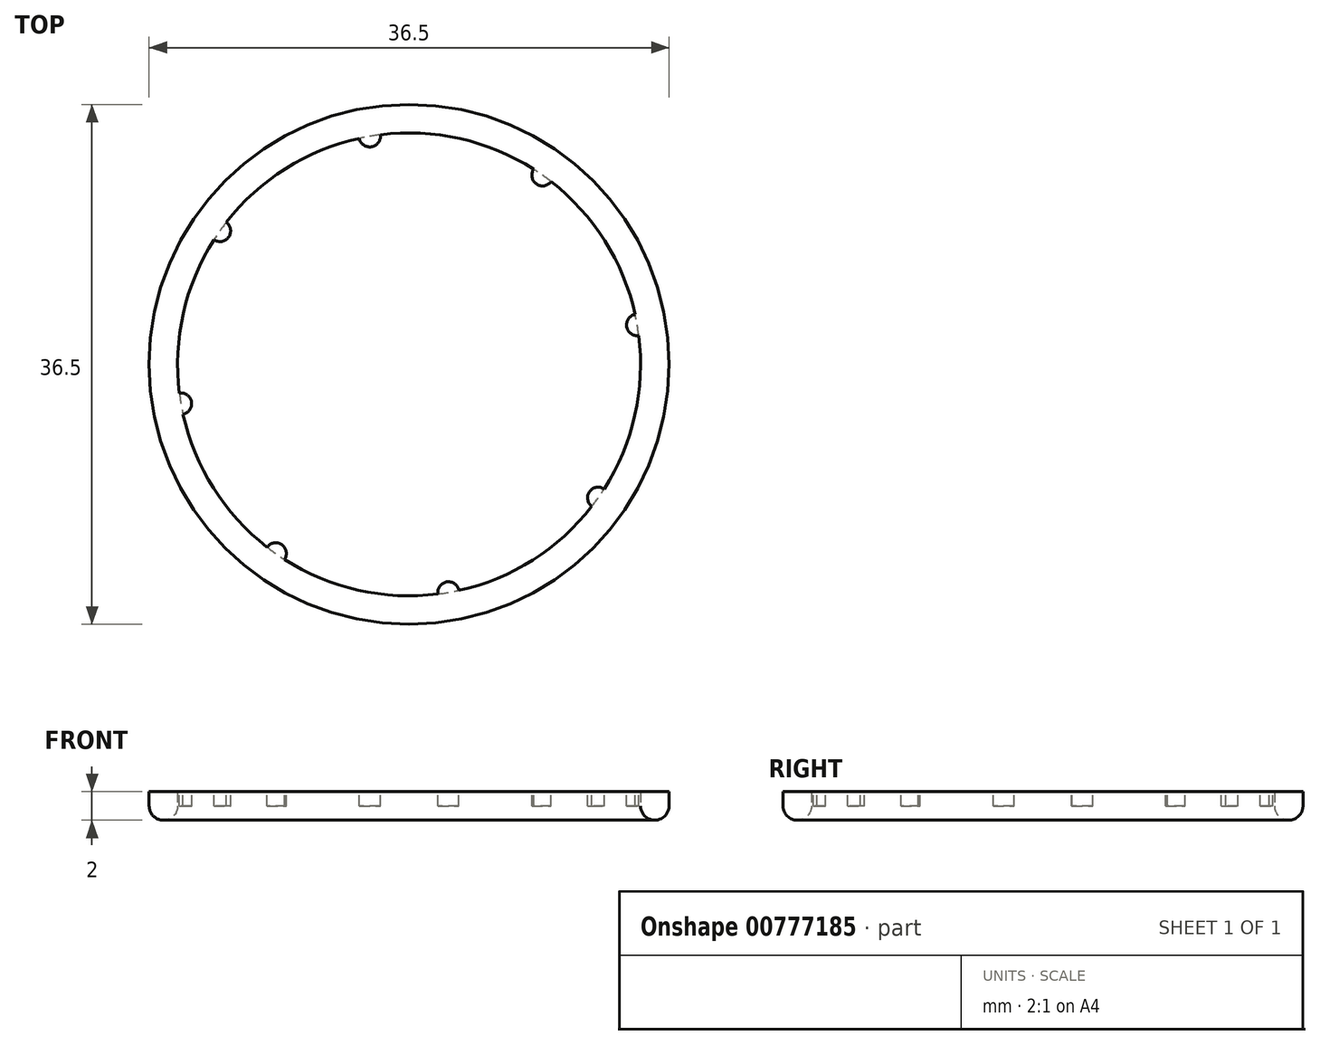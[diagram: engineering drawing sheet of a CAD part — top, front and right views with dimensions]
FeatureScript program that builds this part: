
annotation { "Feature Type Name" : "Feature", "Feature Type Description" : "" }
export const myFeature = defineFeature(function(context is Context, id is Id, definition is map)
    precondition{}
    {
        {
            var Q0;
            Q0=qCreatedBy(makeId("Top.planeOp"),FACE);
            var sketch = newSketch(context, id + "F0", { "sketchPlane" : qUnion([Q0])});
            skCircle(sketch, "E0", {"center": v(0, 0) * mm, "radius": 16.25 * mm});
            skCircle(sketch, "E1.0", {"center": v(0, 0) * mm, "radius": 18.25 * mm});
            skSolve(sketch);
        }
        {
            var Q0;
            Q0=makeQuery(id+"F0.imprint","IMPRINT",FACE,{"disambiguationData":[TD([[makeQuery(id+"F0.imprint","IMPRINT",EDGE,{"derivedFrom":sQuery(id+"F0.wireOp",EDGE,"E0")}),-1.0]])]});
            extrude(context, id + "F1", {"entities" : qUnion([Q0]), "depth" : 2 * mm, "offsetDistance" : 25 * mm});
        }
        {
            var Q0;
            Q0=makeQuery(id+"F1.opExtrude","CAP_FACE",FACE,{"disambiguationData":[OSD([sQuery(id+"F0.wireOp",EDGE,"E0"),sQuery(id+"F0.wireOp",EDGE,"E1.0")])],"isStart":false});
            var sketch = newSketch(context, id + "F2", { "sketchPlane" : qUnion([Q0])});
            skCircle(sketch, "E2", {"center": v(-13.28, 9.37) * mm, "radius": 0.75 * mm});
            skCircle(sketch, "E3.1.0", {"center": v(-16.01, -2.76) * mm, "radius": 0.75 * mm});
            skCircle(sketch, "E3.2.0", {"center": v(-9.37, -13.28) * mm, "radius": 0.75 * mm});
            skPoint(sketch, "E3.center", {"position": v(0, 0) * mm});
            skCircle(sketch, "E4.1.3.0", {"center": v(2.76, -16.01) * mm, "radius": 0.75 * mm});
            skCircle(sketch, "E4.1.4.0", {"center": v(13.28, -9.37) * mm, "radius": 0.75 * mm});
            skCircle(sketch, "E5.1.5.0", {"center": v(16.01, 2.76) * mm, "radius": 0.75 * mm});
            skCircle(sketch, "E5.1.6.0", {"center": v(9.37, 13.28) * mm, "radius": 0.75 * mm});
            skCircle(sketch, "E5.1.7.0", {"center": v(-2.76, 16.01) * mm, "radius": 0.75 * mm});
            skSolve(sketch);
        }
        {
            var Q0;
            {var subQ0=sQuery(id+"F2.wireOp",EDGE,"E5.1.5.0");var subQ1=makeQuery(id+"F1.opExtrude","CAP_EDGE",EDGE,{"disambiguationData":[OSD([sQuery(id+"F0.wireOp",EDGE,"E0")])],"isStart":false});var subQ2=makeQuery(id+"F2.imprint","INTERSECT",VERTEX,{"disambiguationData":[OD(0.0)],"derivedFrom":[subQ1,subQ0]});Q0=makeQuery(id+"F2.imprint","IMPRINT",FACE,{"disambiguationData":[TD([[makeQuery(id+"F2.imprint","IMPRINT",EDGE,{"disambiguationData":[TD([[subQ2,1.0]])],"derivedFrom":subQ0}),1.0]])]});}
            var Q1;
            {var subQ0=sQuery(id+"F2.wireOp",EDGE,"E4.1.4.0");var subQ1=makeQuery(id+"F1.opExtrude","CAP_EDGE",EDGE,{"disambiguationData":[OSD([sQuery(id+"F0.wireOp",EDGE,"E0")])],"isStart":false});var subQ2=makeQuery(id+"F2.imprint","INTERSECT",VERTEX,{"disambiguationData":[OD(0.0)],"derivedFrom":[subQ1,subQ0]});Q1=makeQuery(id+"F2.imprint","IMPRINT",FACE,{"disambiguationData":[TD([[makeQuery(id+"F2.imprint","IMPRINT",EDGE,{"disambiguationData":[TD([[subQ2,1.0]])],"derivedFrom":subQ0}),1.0]])]});}
            var Q2;
            {var subQ0=sQuery(id+"F2.wireOp",EDGE,"E4.1.3.0");var subQ1=makeQuery(id+"F1.opExtrude","CAP_EDGE",EDGE,{"disambiguationData":[OSD([sQuery(id+"F0.wireOp",EDGE,"E0")])],"isStart":false});var subQ2=makeQuery(id+"F2.imprint","INTERSECT",VERTEX,{"disambiguationData":[OD(0.0)],"derivedFrom":[subQ1,subQ0]});Q2=makeQuery(id+"F2.imprint","IMPRINT",FACE,{"disambiguationData":[TD([[makeQuery(id+"F2.imprint","IMPRINT",EDGE,{"disambiguationData":[TD([[subQ2,1.0]])],"derivedFrom":subQ0}),1.0]])]});}
            var Q3;
            {var subQ0=sQuery(id+"F2.wireOp",EDGE,"E3.2.0");var subQ1=makeQuery(id+"F1.opExtrude","CAP_EDGE",EDGE,{"disambiguationData":[OSD([sQuery(id+"F0.wireOp",EDGE,"E0")])],"isStart":false});var subQ2=makeQuery(id+"F2.imprint","INTERSECT",VERTEX,{"disambiguationData":[OD(0.0)],"derivedFrom":[subQ1,subQ0]});Q3=makeQuery(id+"F2.imprint","IMPRINT",FACE,{"disambiguationData":[TD([[makeQuery(id+"F2.imprint","IMPRINT",EDGE,{"disambiguationData":[TD([[subQ2,1.0]])],"derivedFrom":subQ0}),1.0]])]});}
            var Q4;
            {var subQ0=sQuery(id+"F2.wireOp",EDGE,"E3.1.0");var subQ1=makeQuery(id+"F1.opExtrude","CAP_EDGE",EDGE,{"disambiguationData":[OSD([sQuery(id+"F0.wireOp",EDGE,"E0")])],"isStart":false});var subQ2=makeQuery(id+"F2.imprint","INTERSECT",VERTEX,{"disambiguationData":[OD(0.0)],"derivedFrom":[subQ1,subQ0]});Q4=makeQuery(id+"F2.imprint","IMPRINT",FACE,{"disambiguationData":[TD([[makeQuery(id+"F2.imprint","IMPRINT",EDGE,{"disambiguationData":[TD([[subQ2,-1.0]])],"derivedFrom":subQ0}),1.0]])]});}
            var Q5;
            {var subQ0=sQuery(id+"F2.wireOp",EDGE,"E2");var subQ1=makeQuery(id+"F1.opExtrude","CAP_EDGE",EDGE,{"disambiguationData":[OSD([sQuery(id+"F0.wireOp",EDGE,"E0")])],"isStart":false});var subQ2=makeQuery(id+"F2.imprint","INTERSECT",VERTEX,{"disambiguationData":[OD(0.0)],"derivedFrom":[subQ1,subQ0]});Q5=makeQuery(id+"F2.imprint","IMPRINT",FACE,{"disambiguationData":[TD([[makeQuery(id+"F2.imprint","IMPRINT",EDGE,{"disambiguationData":[TD([[subQ2,-1.0]])],"derivedFrom":subQ0}),1.0]])]});}
            var Q6;
            {var subQ0=sQuery(id+"F2.wireOp",EDGE,"E5.1.7.0");var subQ1=makeQuery(id+"F1.opExtrude","CAP_EDGE",EDGE,{"disambiguationData":[OSD([sQuery(id+"F0.wireOp",EDGE,"E0")])],"isStart":false});var subQ2=makeQuery(id+"F2.imprint","INTERSECT",VERTEX,{"disambiguationData":[OD(0.0)],"derivedFrom":[subQ1,subQ0]});Q6=makeQuery(id+"F2.imprint","IMPRINT",FACE,{"disambiguationData":[TD([[makeQuery(id+"F2.imprint","IMPRINT",EDGE,{"disambiguationData":[TD([[subQ2,-1.0]])],"derivedFrom":subQ0}),1.0]])]});}
            var Q7;
            {var subQ0=sQuery(id+"F2.wireOp",EDGE,"E5.1.6.0");var subQ1=makeQuery(id+"F1.opExtrude","CAP_EDGE",EDGE,{"disambiguationData":[OSD([sQuery(id+"F0.wireOp",EDGE,"E0")])],"isStart":false});var subQ2=makeQuery(id+"F2.imprint","INTERSECT",VERTEX,{"disambiguationData":[OD(0.0)],"derivedFrom":[subQ1,subQ0]});Q7=makeQuery(id+"F2.imprint","IMPRINT",FACE,{"disambiguationData":[TD([[makeQuery(id+"F2.imprint","IMPRINT",EDGE,{"disambiguationData":[TD([[subQ2,-1.0]])],"derivedFrom":subQ0}),1.0]])]});}
            extrude(context, id + "F3", {"entities" : qUnion([Q0, Q1, Q2, Q3, Q4, Q5, Q6, Q7]), "operationType" : NewBodyOperationType.ADD, "oppositeDirection" : true, "depth" : 1 * mm, "offsetDistance" : 25 * mm});
        }
        {
            var Q0;
            Q0=makeQuery(id+"F1.opExtrude","CAP_FACE",FACE,{"disambiguationData":[OSD([sQuery(id+"F0.wireOp",EDGE,"E0"),sQuery(id+"F0.wireOp",EDGE,"E1.0")])],"isStart":true});
            fillet(context, id + "F4", {"entities" : qUnion([Q0]), "radius" : 1 * mm, "tangentPropagation" : true, "allowEdgeOverflow" : false});
        }
    });
